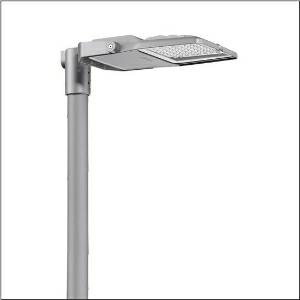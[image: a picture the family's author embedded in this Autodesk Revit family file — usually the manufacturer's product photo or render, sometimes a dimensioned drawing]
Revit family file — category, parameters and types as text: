
# Revit family: floodlight_fl_21_mini___pl52_5xa7776c4d3a_f656
name_source: partatom
category: Lighting Fixtures
units: mm (PartAtom-declared; Revit-internal decimal feet)

## family parameters
Cut with Voids When Loaded = No
Host = Face
Light Source = No
Part Type = Normal
Room Calculation Point = No
Round Connector Dimension = Use Diameter
Shared = No

## types (1)
- --- (1 x LED, 12700 lm, 89 W, 4000K)
    Apparent Load = 89 VA
    CIE Flux Codes = 26 60 98 100 100
    Color Rendering = 70
    Color Temperature = 4000K
    Default Elevation = 1800 mm
    Description = Floodlight FL 21 mini, floodlight, primary light control with lens, of PMMA, primary optical cover: protective disc, of toughened safety glass, transparent, light distribution: PL52, light emission: direct distribution, installation type: surface-mounted, LED, High Power LED, rated luminous flux: 12.700lm, luminous efficacy: 143lm/W, light colour: 740, colour temperature: 4000K, control gear: Smart Interface (Zhaga), control: pre-setting: logarithmic dimming characteristic, flexible luminous flux parameterisation, time-dependent luminous flux control, constant luminous flux control, overheat protection, with terminal, 6-pole, mains connection: 220..240V, AC, 50/60Hz, start of lifetime: 89W, end of service life: 94W, reduction: 43W, luminaire housing, of diecast aluminium, powder-coated, Siteco® metallic grey (DB 702S), corrosivity category C5 mid according to DIN EN ISO 12944, suitable for swimming pools, chlorine-resistant, sealing non-destructively replaceable, please order mast flange separately, mast bracket, of steel, galvanised, powder-coated, Siteco® metallic grey (DB 702S), Smart Interface below and above, protection rating (complete): IP66, insulation class (complete): insulation class II (safety insulation), certification: CE, ENEC, VDE, protection symbol: D, impact resistance: IK08, permissible operating ambient temperature: -40..+40°C, permissible operating ambient temperature for outdoor applications: -40..+50°C, standard: DIN EN 12944, LABS conformity tested according to VDMA 24364:2018-05, packaging unit: 1 piece

Light Distribution: PL52
    Height = 70 mm
    Lamp = 1 x LED
    Lamp Light Flux = 12700 lm
    Lamp Power = 89 W
    Lamp count = 1
    Length = 485 mm
    Luminous efficacy = 143 lm/W
    Manufacturer = Siteco
    ModVariant = No
    Model = 5XA7776C4D3A
    Number of Poles = 1
    OnlyDefault = Yes
    Power Factor = 1
    Product Name = Floodlight FL 21 mini | PL52
    Product group = floodlight | pylon annexe
    ProductGroupID = 6200
    Protection Class = Protection class II
    Protection Degree = IP 66
    RLX_Detail_Level = 1
    RLX_Emergency_Light_Flux = 0 lm
    RLX_Emergency_Type = 0
    RLX_Emergency_Type_DB = No
    RlxData = <blob elided: 101161 chars, md5=89628da7>
    Socket = socket
    Standby Power = 0 W
    System Light Flux = 12700 lm
    System Power = 89 W
    Type Comments = factory setting: luminous flux: 100 % | dim-lin: 254 | 456 mA
    Type Image = l_1007125.jpg
    URL = http://relux.com
    VarID = @adj_027154
    Voltage = 0 V
    Weight = 0.00 kg
    Width = 337 mm

## geometry (parser evidence)
native form markers: Blend x4, Sweep x12
no freeform markers — native parametric forms only
